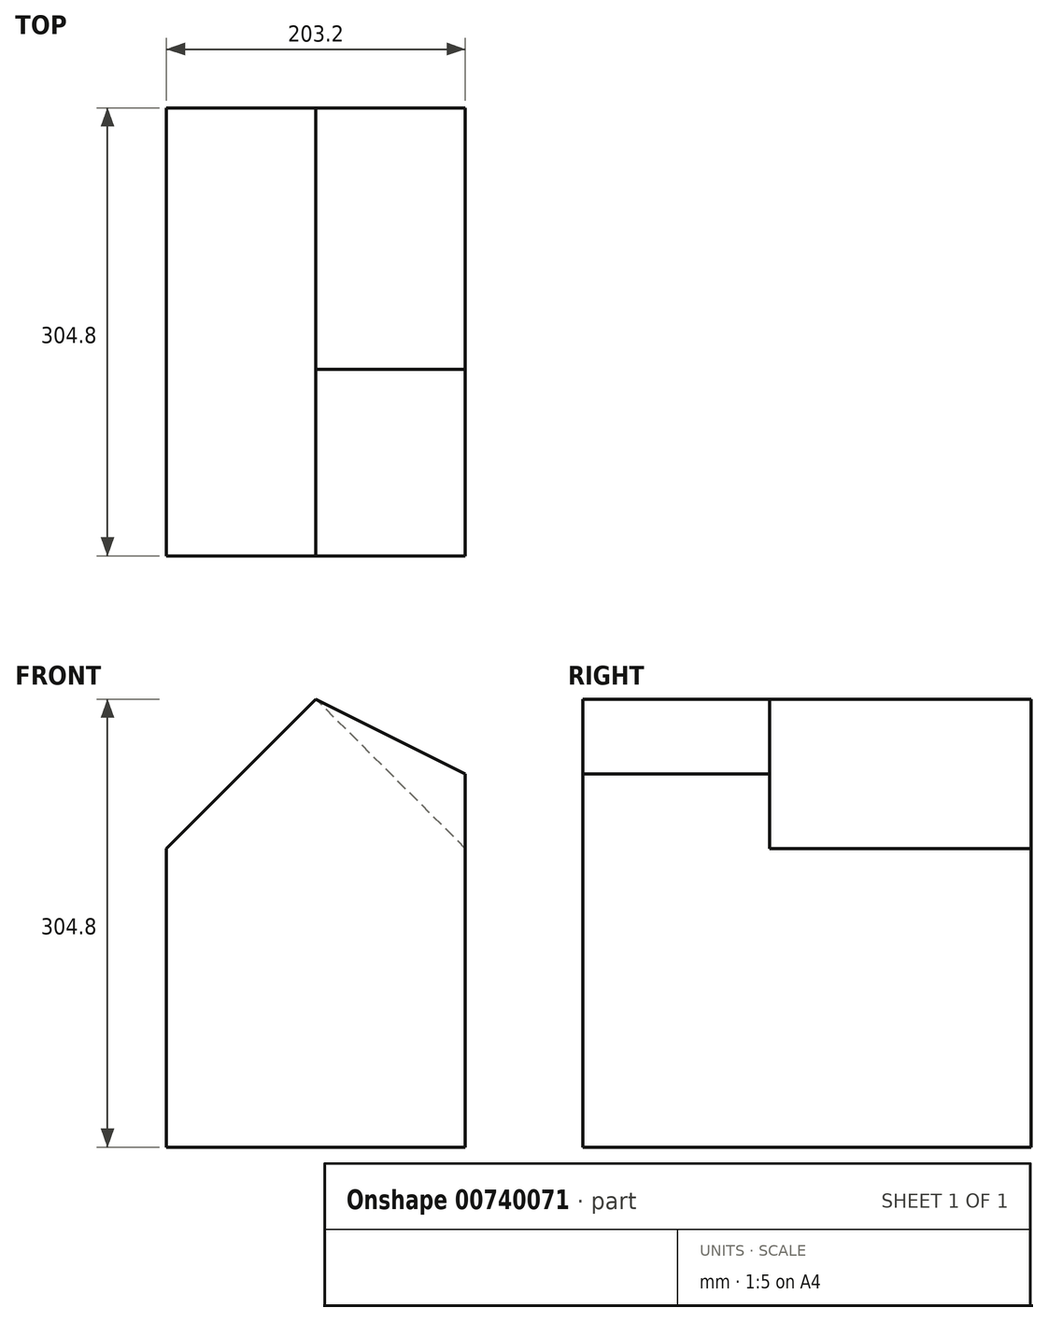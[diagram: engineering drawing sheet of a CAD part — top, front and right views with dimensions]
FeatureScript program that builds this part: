
annotation { "Feature Type Name" : "Feature", "Feature Type Description" : "" }
export const myFeature = defineFeature(function(context is Context, id is Id, definition is map)
    precondition{}
    {
        {
            var Q0;
            Q0=qCreatedBy(makeId("Front.planeOp"),FACE);
            var sketch = newSketch(context, id + "F0", { "sketchPlane" : qUnion([Q0])});
            skLineSegment(sketch, "E0.bottom", {"start": v(-101.6, 101.6) * mm, "end": v(101.6, 101.6) * mm});
            skLineSegment(sketch, "E0.top", {"start": v(-101.6, -101.6) * mm, "end": v(101.6, -101.6) * mm});
            skLineSegment(sketch, "E0.left", {"start": v(-101.6, 101.6) * mm, "end": v(-101.6, -101.6) * mm});
            skLineSegment(sketch, "E0.right", {"start": v(101.6, 101.6) * mm, "end": v(101.6, -101.6) * mm});
            skPoint(sketch, "E0.middle", {"position": v(0, 0) * mm});
            skSolve(sketch);
        }
        {
            var Q0;
            Q0=makeQuery(id+"F0.imprint","IMPRINT",FACE,{"disambiguationData":[TD([[makeQuery(id+"F0.imprint","IMPRINT",EDGE,{"derivedFrom":sQuery(id+"F0.wireOp",EDGE,"E0.bottom")}),-1.0]])]});
            extrude(context, id + "F1", {"entities" : qUnion([Q0]), "depth" : 177.8 * mm, "offsetDistance" : 25.4 * mm});
        }
        {
            var Q0;
            Q0=makeQuery(id+"F1.opExtrude","CAP_FACE",FACE,{"disambiguationData":[OSD([sQuery(id+"F0.wireOp",EDGE,"E0.bottom"),sQuery(id+"F0.wireOp",EDGE,"E0.top"),sQuery(id+"F0.wireOp",EDGE,"E0.left"),sQuery(id+"F0.wireOp",EDGE,"E0.right")])],"isStart":true});
            var sketch = newSketch(context, id + "F2", { "sketchPlane" : qUnion([Q0])});
            skLineSegment(sketch, "E1", {"start": v(-101.6, 101.6) * mm, "end": v(0, 203.2) * mm});
            skLineSegment(sketch, "E2", {"start": v(0, 203.2) * mm, "end": v(101.6, 101.6) * mm});
            skLineSegment(sketch, "E3", {"start": v(101.6, 101.6) * mm, "end": v(-101.6, 101.6) * mm});
            skSolve(sketch);
        }
        {
            var Q0;
            Q0=makeQuery(id+"F2.imprint","IMPRINT",FACE,{"disambiguationData":[TD([[makeQuery(id+"F2.imprint","IMPRINT",EDGE,{"derivedFrom":sQuery(id+"F2.wireOp",EDGE,"E1")}),-1.0]])]});
            extrude(context, id + "F3", {"entities" : qUnion([Q0]), "operationType" : NewBodyOperationType.ADD, "oppositeDirection" : true, "depth" : 177.8 * mm, "offsetDistance" : 25.4 * mm});
        }
        {
            var Q0;
            Q0=makeQuery(id+"F3.boolean.opBoolean","MERGE",FACE,{"derivedFrom":[makeQuery(id+"F1.opExtrude","CAP_FACE",FACE,{"disambiguationData":[OSD([sQuery(id+"F0.wireOp",EDGE,"E0.bottom"),sQuery(id+"F0.wireOp",EDGE,"E0.top"),sQuery(id+"F0.wireOp",EDGE,"E0.left"),sQuery(id+"F0.wireOp",EDGE,"E0.right")])],"isStart":false}),makeQuery(id+"F3.opExtrude","CAP_FACE",FACE,{"disambiguationData":[OSD([sQuery(id+"F2.wireOp",EDGE,"E1"),sQuery(id+"F2.wireOp",EDGE,"E2"),sQuery(id+"F2.wireOp",EDGE,"E3")])],"isStart":false})]});
            var sketch = newSketch(context, id + "F4", { "sketchPlane" : qUnion([Q0])});
            skLineSegment(sketch, "E4", {"start": v(-101.6, 50.8) * mm, "end": v(101.6, 50.8) * mm});
            skLineSegment(sketch, "E5", {"start": v(101.6, 50.8) * mm, "end": v(101.6, -101.6) * mm});
            skLineSegment(sketch, "E6", {"start": v(101.6, -101.6) * mm, "end": v(-101.6, -101.6) * mm});
            skLineSegment(sketch, "E7", {"start": v(-101.6, -101.6) * mm, "end": v(-101.6, 50.8) * mm});
            skLineSegment(sketch, "E8", {"start": v(-101.6, 50.8) * mm, "end": v(-101.6, 101.6) * mm});
            skLineSegment(sketch, "E9", {"start": v(-101.6, 101.6) * mm, "end": v(0, 203.2) * mm});
            skLineSegment(sketch, "E10", {"start": v(0, 203.2) * mm, "end": v(101.6, 152.4) * mm});
            skLineSegment(sketch, "E11", {"start": v(101.6, 152.4) * mm, "end": v(101.6, 50.8) * mm});
            skSolve(sketch);
        }
        {
            var Q0;
            Q0=makeQuery(id+"F4.imprint","IMPRINT",FACE,{"disambiguationData":[TD([[makeQuery(id+"F4.imprint","IMPRINT",EDGE,{"derivedFrom":sQuery(id+"F4.wireOp",EDGE,"E4")}),-1.0]])]});
            extrude(context, id + "F5", {"entities" : qUnion([Q0]), "operationType" : NewBodyOperationType.ADD, "depth" : 127 * mm, "offsetDistance" : 25.4 * mm});
        }
        {
            var Q0;
            {var subQ2=sQuery(id+"F4.wireOp",EDGE,"E4");Q0=makeQuery(id+"F4.imprint","IMPRINT",FACE,{"disambiguationData":[TD([[makeQuery(id+"F4.imprint","IMPRINT",EDGE,{"derivedFrom":subQ2}),1.0]])]});}
            var Q1;
            {var subQ0=sQuery(id+"F4.wireOp",EDGE,"E10");Q1=makeQuery(id+"F4.imprint","IMPRINT",FACE,{"disambiguationData":[TD([[makeQuery(id+"F4.imprint","IMPRINT",EDGE,{"derivedFrom":subQ0}),-1.0]])]});}
            extrude(context, id + "F6", {"entities" : qUnion([Q0, Q1]), "operationType" : NewBodyOperationType.ADD, "depth" : 127 * mm, "offsetDistance" : 25.4 * mm});
        }
    });
